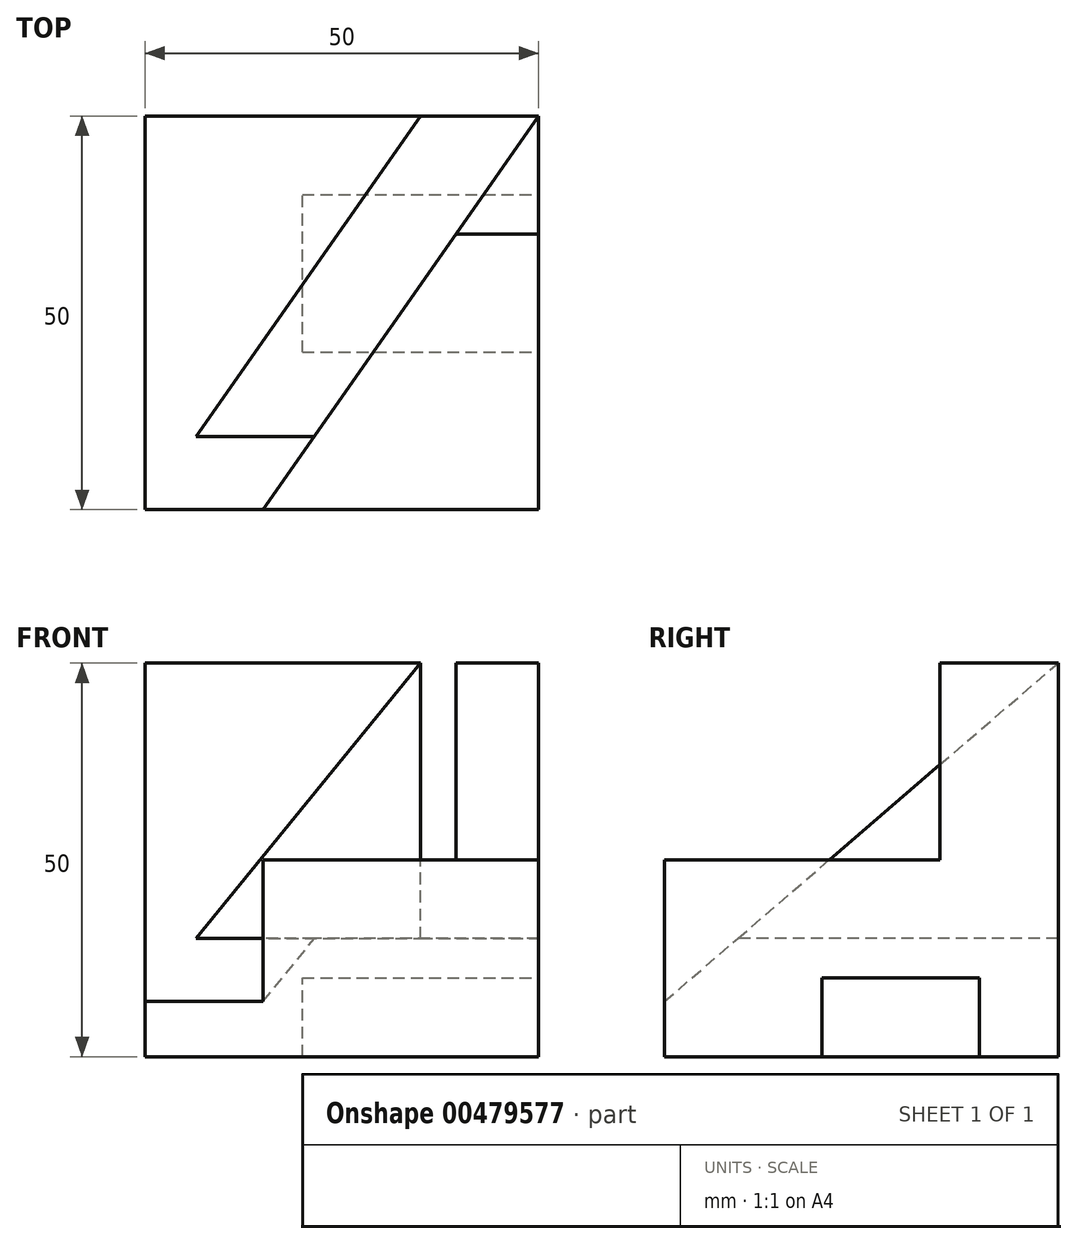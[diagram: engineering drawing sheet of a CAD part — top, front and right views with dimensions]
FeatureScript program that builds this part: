
annotation { "Feature Type Name" : "Feature", "Feature Type Description" : "" }
export const myFeature = defineFeature(function(context is Context, id is Id, definition is map)
    precondition{}
    {
        {
            var Q0;
            Q0=qCreatedBy(makeId("Top.planeOp"),FACE);
            var sketch = newSketch(context, id + "F0", { "sketchPlane" : qUnion([Q0])});
            skLineSegment(sketch, "E0.bottom", {"start": v(0, 0) * mm, "end": v(50, 0) * mm});
            skLineSegment(sketch, "E0.top", {"start": v(0, 50) * mm, "end": v(50, 50) * mm});
            skLineSegment(sketch, "E0.left", {"start": v(0, 0) * mm, "end": v(0, 50) * mm});
            skLineSegment(sketch, "E0.right", {"start": v(50, 0) * mm, "end": v(50, 50) * mm});
            skSolve(sketch);
        }
        {
            var Q0;
            Q0 = qSketchRegion(id + "F0", true);
            extrude(context, id + "F1", {"entities" : qUnion([Q0]), "depth" : 50 * mm});
        }
        {
            var Q0;
            Q0=makeQuery(id+"F1.opExtrude","SWEPT_FACE",FACE,{"disambiguationData":[OSD([sQuery(id+"F0.wireOp",EDGE,"E0.right")])]});
            var sketch = newSketch(context, id + "F2", { "sketchPlane" : qUnion([Q0])});
            skLineSegment(sketch, "E1.bottom", {"start": v(20, 0) * mm, "end": v(40, 0) * mm});
            skLineSegment(sketch, "E1.top", {"start": v(20, 10) * mm, "end": v(40, 10) * mm});
            skLineSegment(sketch, "E1.left", {"start": v(20, 0) * mm, "end": v(20, 10) * mm});
            skLineSegment(sketch, "E1.right", {"start": v(40, 0) * mm, "end": v(40, 10) * mm});
            skSolve(sketch);
        }
        {
            var Q0;
            Q0=makeQuery(id+"F2.imprint","IMPRINT",FACE,{"disambiguationData":[TD([[makeQuery(id+"F2.imprint","IMPRINT",EDGE,{"derivedFrom":sQuery(id+"F2.wireOp",EDGE,"E1.bottom")}),1.0]])]});
            extrude(context, id + "F3", {"entities" : qUnion([Q0]), "operationType" : NewBodyOperationType.REMOVE, "oppositeDirection" : true, "depth" : 30 * mm});
        }
        {
            var Q0;
            Q0=makeQuery(id+"F1.opExtrude","CAP_FACE",FACE,{"disambiguationData":[OSD([sQuery(id+"F0.wireOp",EDGE,"E0.bottom"),sQuery(id+"F0.wireOp",EDGE,"E0.top"),sQuery(id+"F0.wireOp",EDGE,"E0.left"),sQuery(id+"F0.wireOp",EDGE,"E0.right")])],"isStart":false});
            var sketch = newSketch(context, id + "F4", { "sketchPlane" : qUnion([Q0])});
            skLineSegment(sketch, "E2", {"start": v(50, 50) * mm, "end": v(15, 0) * mm});
            skLineSegment(sketch, "E3", {"start": v(50, 50) * mm, "end": v(35, 50) * mm});
            skLineSegment(sketch, "E4", {"start": v(50, 50) * mm, "end": v(50, 35) * mm});
            skLineSegment(sketch, "E5", {"start": v(50, 35) * mm, "end": v(39.5, 35) * mm});
            skSolve(sketch);
        }
        {
            var Q0;
            {var subQ3=sQuery(id+"F4.wireOp",EDGE,"E5");Q0=makeQuery(id+"F4.imprint","IMPRINT",FACE,{"disambiguationData":[TD([[makeQuery(id+"F4.imprint","IMPRINT",EDGE,{"derivedFrom":subQ3}),1.0]])]});}
            extrude(context, id + "F5", {"entities" : qUnion([Q0]), "operationType" : NewBodyOperationType.REMOVE, "oppositeDirection" : true, "depth" : 25 * mm});
        }
        {
            var Q0;
            Q0=makeQuery(id+"F1.opExtrude","CAP_FACE",FACE,{"disambiguationData":[OSD([sQuery(id+"F0.wireOp",EDGE,"E0.bottom"),sQuery(id+"F0.wireOp",EDGE,"E0.top"),sQuery(id+"F0.wireOp",EDGE,"E0.left"),sQuery(id+"F0.wireOp",EDGE,"E0.right")])],"isStart":false});
            var sketch = newSketch(context, id + "F6", { "sketchPlane" : qUnion([Q0])});
            skLineSegment(sketch, "E6", {"start": v(50, 50) * mm, "end": v(15, 0) * mm});
            skLineSegment(sketch, "E7", {"start": v(15, 0) * mm, "end": v(0, 0) * mm});
            skLineSegment(sketch, "E8", {"start": v(0, 0) * mm, "end": v(35, 50) * mm});
            skLineSegment(sketch, "E9", {"start": v(35, 50) * mm, "end": v(50, 50) * mm});
            skSolve(sketch);
        }
        {
            var Q0;
            {var subQ0=sQuery(id+"F6.wireOp",EDGE,"E7");Q0=makeQuery(id+"F6.imprint","IMPRINT",FACE,{"disambiguationData":[TD([[makeQuery(id+"F6.imprint","IMPRINT",EDGE,{"derivedFrom":subQ0}),1.0]])]});}
            extrude(context, id + "F7", {"entities" : qUnion([Q0]), "operationType" : NewBodyOperationType.REMOVE, "oppositeDirection" : true, "depth" : 35 * mm});
        }
        {
            var Q0;
            Q0=makeQuery(id+"F1.opExtrude","SWEPT_FACE",FACE,{"disambiguationData":[OSD([sQuery(id+"F0.wireOp",EDGE,"E0.left")])]});
            var sketch = newSketch(context, id + "F8", { "sketchPlane" : qUnion([Q0])});
            skLineSegment(sketch, "E10", {"start": v(-50, 7) * mm, "end": v(0, 7) * mm});
            skLineSegment(sketch, "E11", {"start": v(-50, 50) * mm, "end": v(0, 7) * mm});
            skSolve(sketch);
        }
        {
            var Q0;
            {var subQ0=sQuery(id+"F8.wireOp",EDGE,"E11");Q0=makeQuery(id+"F8.imprint","IMPRINT",FACE,{"disambiguationData":[TD([[makeQuery(id+"F8.imprint","IMPRINT",EDGE,{"derivedFrom":subQ0}),1.0]])]});}
            var Q1;
            Q1=makeQuery(id+"F7.boolean.opBoolean","COPY",FACE,{"derivedFrom":makeQuery(id+"F7.opExtrude","SWEPT_FACE",FACE,{"disambiguationData":[OSD([sQuery(id+"F6.wireOp",EDGE,"E6")])]})});
            extrude(context, id + "F9", {"entities" : qUnion([Q0]), "operationType" : NewBodyOperationType.REMOVE, "endBound" : BoundingType.UP_TO_SURFACE, "oppositeDirection" : true, "endBoundEntityFace" : qUnion([Q1]), "depth" : 25 * mm});
        }
    });
